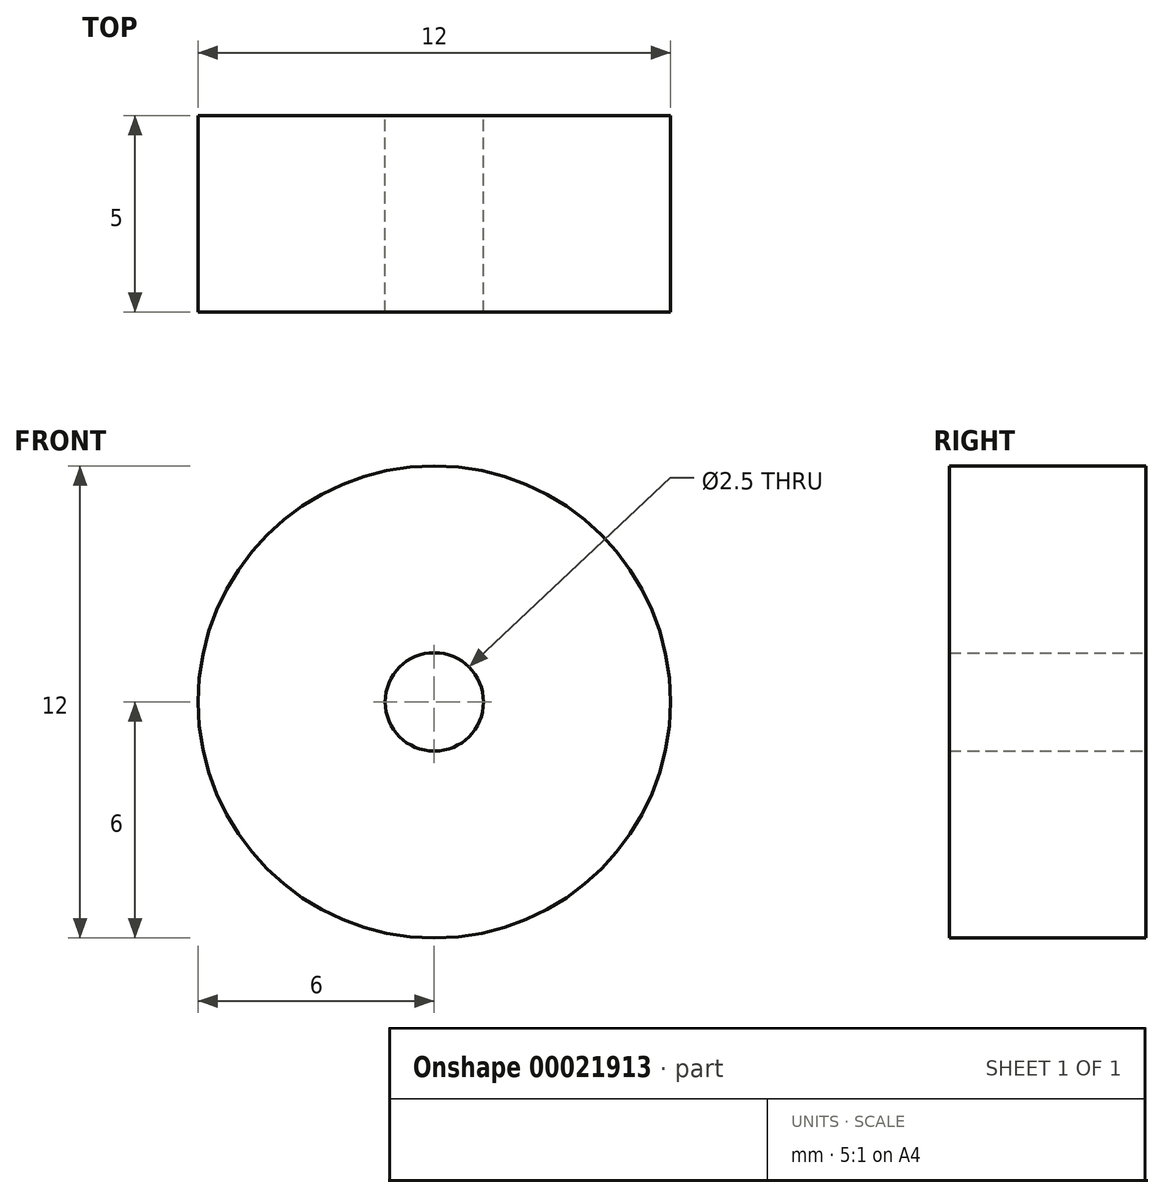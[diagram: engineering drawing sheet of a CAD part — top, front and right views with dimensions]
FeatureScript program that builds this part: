
annotation { "Feature Type Name" : "Feature", "Feature Type Description" : "" }
export const myFeature = defineFeature(function(context is Context, id is Id, definition is map)
    precondition{}
    {
        {
            var Q0;
            Q0=qCreatedBy(makeId("Front.planeOp"),FACE);
            var sketch = newSketch(context, id + "F0", { "sketchPlane" : qUnion([Q0])});
            skCircle(sketch, "E0", {"center": v(0, 0) * mm, "radius": 6 * mm});
            skSolve(sketch);
        }
        {
            var Q0;
            Q0 = qSketchRegion(id + "F0", true);
            extrude(context, id + "F1", {"entities" : qUnion([Q0]), "depth" : 5 * mm});
        }
        {
            var Q0;
            Q0=makeQuery(id+"F1.opExtrude","CAP_FACE",FACE,{"disambiguationData":[OSD([sQuery(id+"F0.wireOp",EDGE,"E0")])],"isStart":true});
            var sketch = newSketch(context, id + "F2", { "sketchPlane" : qUnion([Q0])});
            skCircle(sketch, "E1", {"center": v(0, 0) * mm, "radius": 1.25 * mm});
            skSolve(sketch);
        }
        {
            var Q0;
            Q0 = qSketchRegion(id + "F2", true);
            extrude(context, id + "F3", {"entities" : qUnion([Q0]), "operationType" : NewBodyOperationType.REMOVE, "endBound" : BoundingType.THROUGH_ALL, "oppositeDirection" : true, "depth" : 25.4 * mm});
        }
    });
